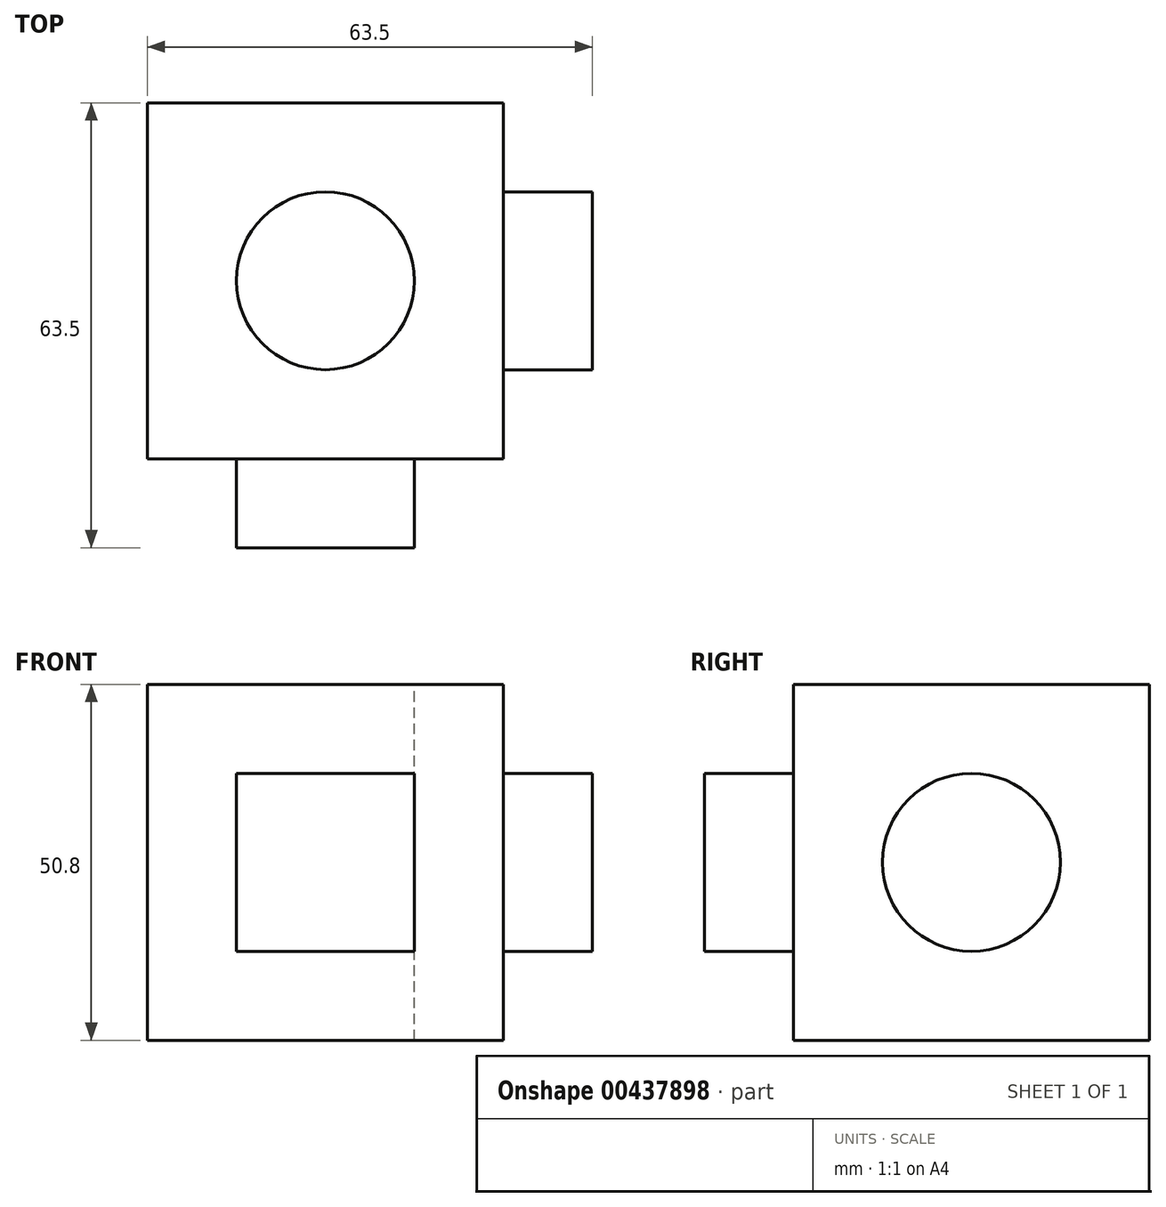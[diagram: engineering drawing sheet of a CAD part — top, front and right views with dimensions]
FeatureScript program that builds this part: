
annotation { "Feature Type Name" : "Feature", "Feature Type Description" : "" }
export const myFeature = defineFeature(function(context is Context, id is Id, definition is map)
    precondition{}
    {
        {
            var Q0;
            Q0=qCreatedBy(makeId("Front.planeOp"),FACE);
            var sketch = newSketch(context, id + "F0", { "sketchPlane" : qUnion([Q0])});
            skLineSegment(sketch, "E0", {"start": v(0, 0) * mm, "end": v(0, 50.8) * mm});
            skLineSegment(sketch, "E1", {"start": v(0, 50.8) * mm, "end": v(0, 0) * mm});
            skLineSegment(sketch, "E2", {"start": v(0, 0) * mm, "end": v(50.8, 0) * mm});
            skLineSegment(sketch, "E3", {"start": v(50.8, 0) * mm, "end": v(50.8, 50.8) * mm});
            skLineSegment(sketch, "E4", {"start": v(50.8, 50.8) * mm, "end": v(0, 50.8) * mm});
            skSolve(sketch);
        }
        {
            var Q0;
            Q0 = qSketchRegion(id + "F0", true);
            extrude(context, id + "F1", {"entities" : qUnion([Q0]), "depth" : 50.8 * mm});
        }
        {
            var Q0;
            Q0=makeQuery(id+"F1.opExtrude","SWEPT_FACE",FACE,{"disambiguationData":[OSD([sQuery(id+"F0.wireOp",EDGE,"E3")])]});
            var sketch = newSketch(context, id + "F2", { "sketchPlane" : qUnion([Q0])});
            skCircle(sketch, "E5", {"center": v(-25.4, 25.4) * mm, "radius": 12.7 * mm});
            skPoint(sketch, "E5.centerSnap0", {"position": v(0, 25.4) * mm});
            skPoint(sketch, "E5.centerSnap1", {"position": v(-25.4, 50.8) * mm});
            skSolve(sketch);
        }
        {
            var Q0;
            Q0 = qSketchRegion(id + "F2", true);
            extrude(context, id + "F3", {"entities" : qUnion([Q0]), "operationType" : NewBodyOperationType.ADD, "depth" : 12.7 * mm});
        }
        {
            var Q0;
            Q0=makeQuery(id+"F1.opExtrude","SWEPT_FACE",FACE,{"disambiguationData":[OSD([sQuery(id+"F0.wireOp",EDGE,"E4")])]});
            var sketch = newSketch(context, id + "F4", { "sketchPlane" : qUnion([Q0])});
            skCircle(sketch, "E6", {"center": v(25.4, -25.4) * mm, "radius": 12.7 * mm});
            skPoint(sketch, "E6.centerSnap0", {"position": v(0, -25.4) * mm});
            skPoint(sketch, "E6.centerSnap1", {"position": v(25.4, 0) * mm});
            skSolve(sketch);
        }
        {
            var Q0;
            Q0 = qSketchRegion(id + "F4", true);
            extrude(context, id + "F5", {"entities" : qUnion([Q0]), "operationType" : NewBodyOperationType.REMOVE, "oppositeDirection" : true, "depth" : 50.8 * mm});
        }
        {
            var Q0;
            Q0=makeQuery(id+"F1.opExtrude","CAP_FACE",FACE,{"disambiguationData":[OSD([sQuery(id+"F0.wireOp",EDGE,"E1"),sQuery(id+"F0.wireOp",EDGE,"E2"),sQuery(id+"F0.wireOp",EDGE,"E3"),sQuery(id+"F0.wireOp",EDGE,"E4")])],"isStart":false});
            var sketch = newSketch(context, id + "F6", { "sketchPlane" : qUnion([Q0])});
            skLineSegment(sketch, "E7.bottom", {"start": v(12.7, 38.1) * mm, "end": v(38.1, 38.1) * mm});
            skLineSegment(sketch, "E7.top", {"start": v(12.7, 12.7) * mm, "end": v(38.1, 12.7) * mm});
            skLineSegment(sketch, "E7.left", {"start": v(12.7, 38.1) * mm, "end": v(12.7, 12.7) * mm});
            skLineSegment(sketch, "E7.right", {"start": v(38.1, 38.1) * mm, "end": v(38.1, 12.7) * mm});
            skSolve(sketch);
        }
        {
            var Q0;
            Q0 = qSketchRegion(id + "F6", true);
            extrude(context, id + "F7", {"entities" : qUnion([Q0]), "operationType" : NewBodyOperationType.ADD, "depth" : 12.7 * mm});
        }
    });
